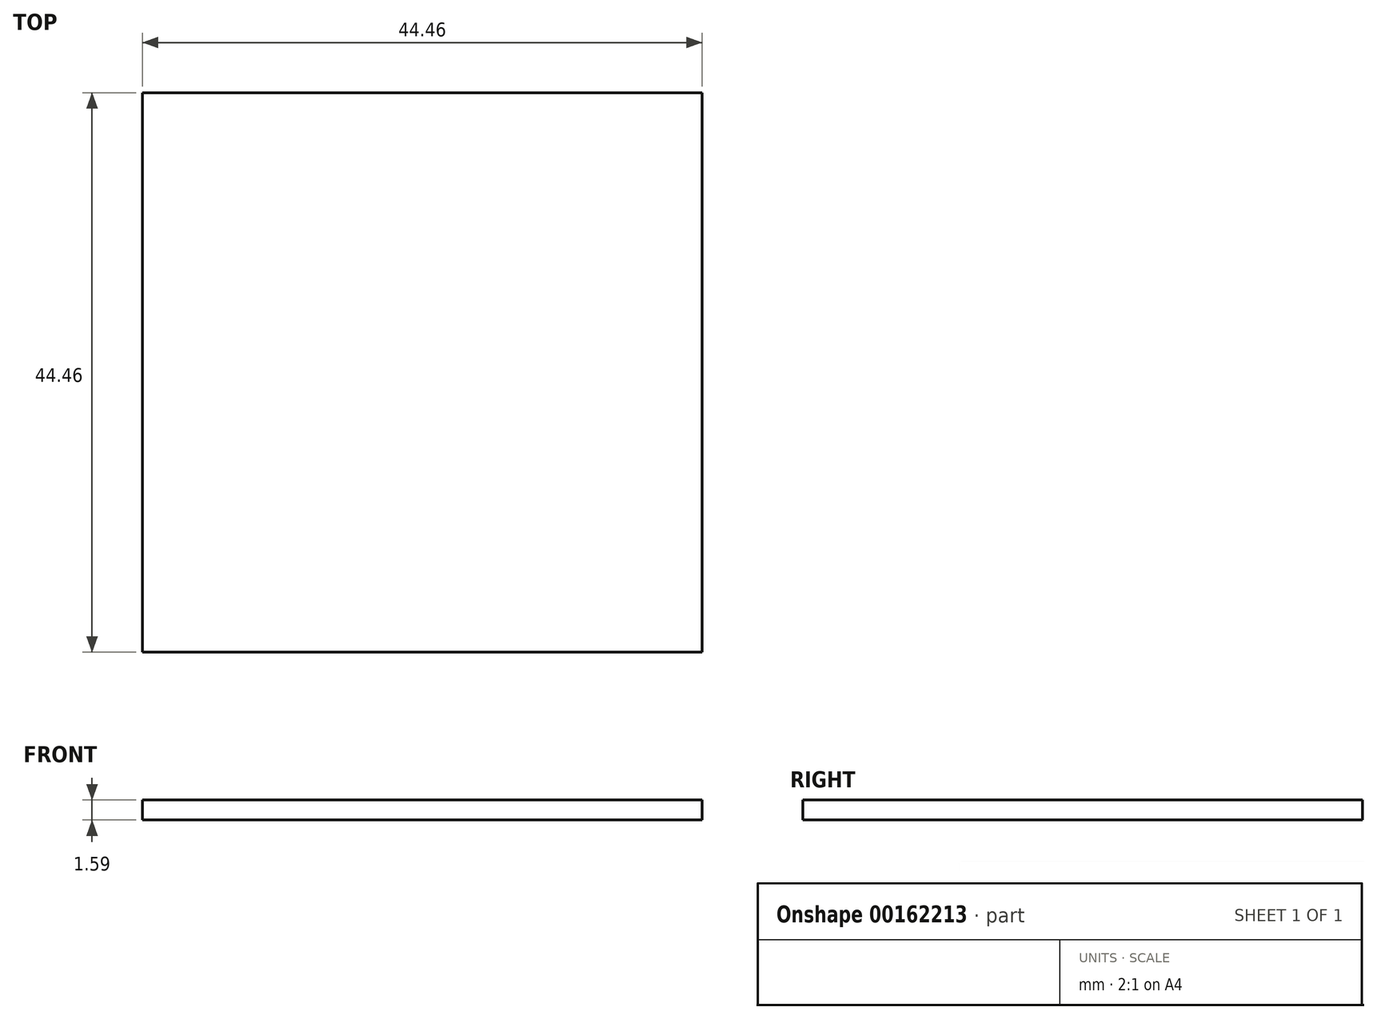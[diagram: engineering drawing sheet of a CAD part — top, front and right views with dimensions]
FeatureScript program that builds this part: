
annotation { "Feature Type Name" : "Feature", "Feature Type Description" : "" }
export const myFeature = defineFeature(function(context is Context, id is Id, definition is map)
    precondition{}
    {
        {
            var Q0;
            Q0=qCreatedBy(makeId("Top.planeOp"),FACE);
            var sketch = newSketch(context, id + "F0", { "sketchPlane" : qUnion([Q0])});
            skLineSegment(sketch, "E0.bottom", {"start": v(-22.22, 22.23) * mm, "end": v(22.23, 22.23) * mm});
            skLineSegment(sketch, "E0.top", {"start": v(-22.23, -22.23) * mm, "end": v(22.23, -22.23) * mm});
            skLineSegment(sketch, "E0.left", {"start": v(-22.22, 22.23) * mm, "end": v(-22.23, -22.23) * mm});
            skLineSegment(sketch, "E0.right", {"start": v(22.23, 22.23) * mm, "end": v(22.23, -22.23) * mm});
            skPoint(sketch, "E0.middle", {"position": v(0, 0) * mm});
            skSolve(sketch);
        }
        {
            var Q0;
            Q0 = qSketchRegion(id + "F0", true);
            extrude(context, id + "F1", {"entities" : qUnion([Q0]), "depth" : 1.59 * mm});
        }
    });
